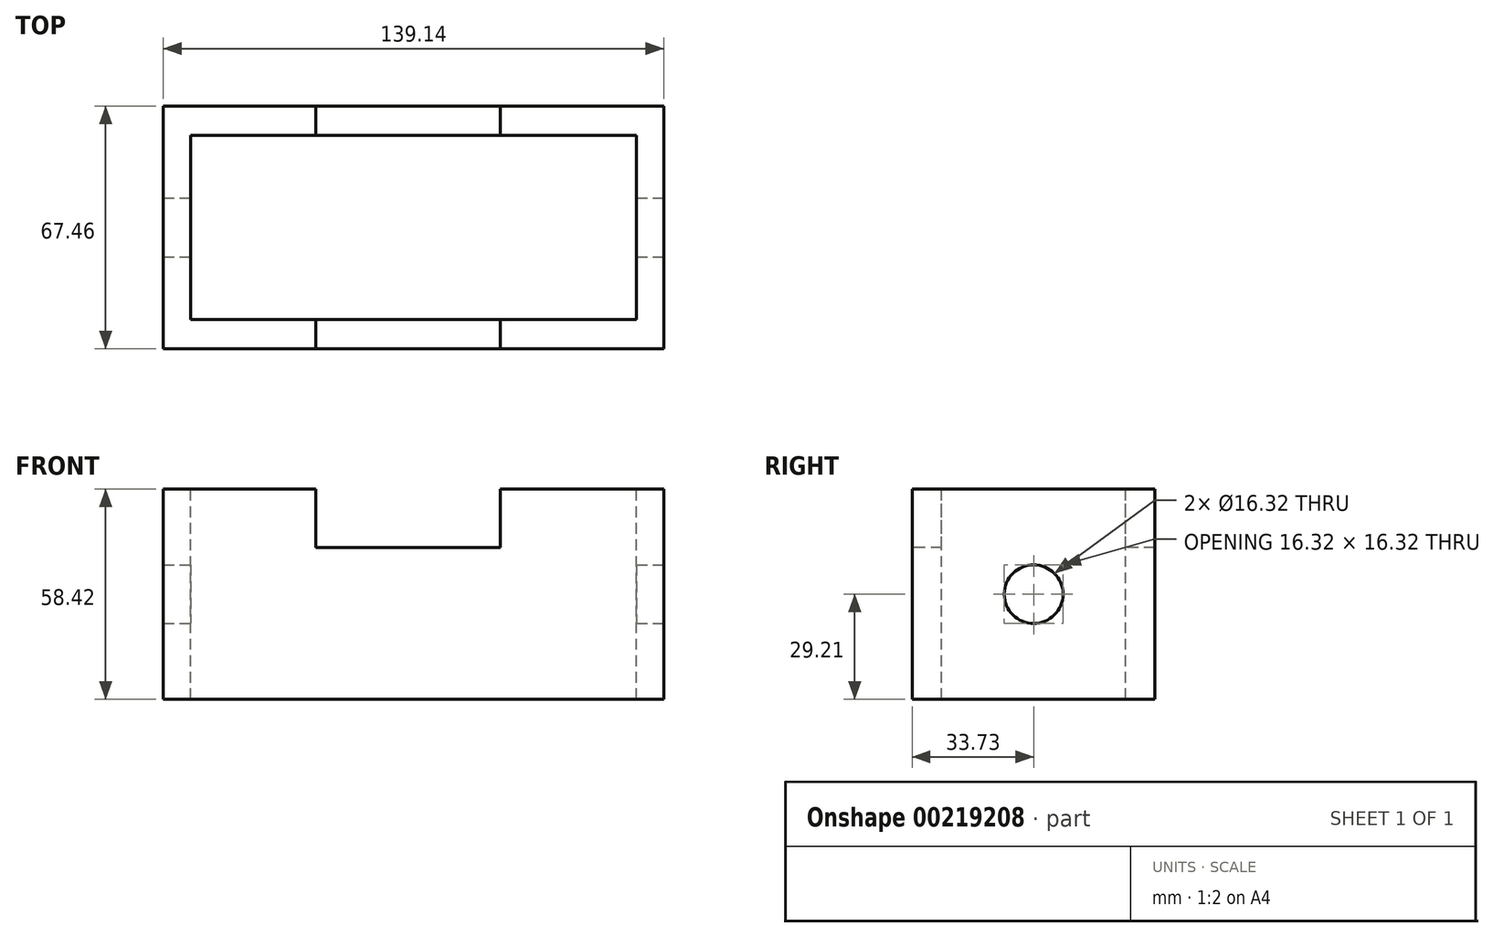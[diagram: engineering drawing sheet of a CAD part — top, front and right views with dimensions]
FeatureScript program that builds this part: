
annotation { "Feature Type Name" : "Feature", "Feature Type Description" : "" }
export const myFeature = defineFeature(function(context is Context, id is Id, definition is map)
    precondition{}
    {
        {
            var Q0;
            Q0=qCreatedBy(makeId("Top.planeOp"),FACE);
            var sketch = newSketch(context, id + "F0", { "sketchPlane" : qUnion([Q0])});
            skLineSegment(sketch, "E0.bottom", {"start": v(69.57, 33.73) * mm, "end": v(-69.57, 33.73) * mm});
            skLineSegment(sketch, "E0.top", {"start": v(69.57, -33.73) * mm, "end": v(-69.57, -33.73) * mm});
            skLineSegment(sketch, "E0.left", {"start": v(69.57, 33.73) * mm, "end": v(69.57, -33.73) * mm});
            skLineSegment(sketch, "E0.right", {"start": v(-69.57, 33.73) * mm, "end": v(-69.57, -33.73) * mm});
            skPoint(sketch, "E0.middle", {"position": v(0, 0) * mm});
            skSolve(sketch);
        }
        {
            var Q0;
            Q0 = qSketchRegion(id + "F0", true);
            extrude(context, id + "F1", {"entities" : qUnion([Q0]), "depth" : 58.42 * mm});
        }
        {
            var Q0;
            Q0=makeQuery(id+"F1.opExtrude","SWEPT_FACE",FACE,{"disambiguationData":[OSD([sQuery(id+"F0.wireOp",EDGE,"E0.left")])]});
            var sketch = newSketch(context, id + "F2", { "sketchPlane" : qUnion([Q0])});
            skCircle(sketch, "E1", {"center": v(0, 29.21) * mm, "radius": 8.16 * mm});
            skPoint(sketch, "E1.centerSnap0", {"position": v(-33.73, 29.21) * mm});
            skSolve(sketch);
        }
        {
            var Q0;
            Q0 = qSketchRegion(id + "F2", true);
            extrude(context, id + "F3", {"entities" : qUnion([Q0]), "operationType" : NewBodyOperationType.REMOVE, "endBound" : BoundingType.THROUGH_ALL, "oppositeDirection" : true, "depth" : 25.4 * mm});
        }
        {
            var Q0;
            Q0=makeQuery(id+"F1.opExtrude","CAP_FACE",FACE,{"disambiguationData":[OSD([sQuery(id+"F0.wireOp",EDGE,"E0.bottom"),sQuery(id+"F0.wireOp",EDGE,"E0.top"),sQuery(id+"F0.wireOp",EDGE,"E0.left"),sQuery(id+"F0.wireOp",EDGE,"E0.right")])],"isStart":false});
            var sketch = newSketch(context, id + "F4", { "sketchPlane" : qUnion([Q0])});
            skLineSegment(sketch, "E2.bottom", {"start": v(62.01, 25.56) * mm, "end": v(-62.01, 25.56) * mm});
            skLineSegment(sketch, "E2.top", {"start": v(62.01, -25.56) * mm, "end": v(-62.01, -25.56) * mm});
            skLineSegment(sketch, "E2.left", {"start": v(62.01, 25.56) * mm, "end": v(62.01, -25.56) * mm});
            skLineSegment(sketch, "E2.right", {"start": v(-62.01, 25.56) * mm, "end": v(-62.01, -25.56) * mm});
            skPoint(sketch, "E2.middle", {"position": v(0, 0) * mm});
            skSolve(sketch);
        }
        {
            var Q0;
            Q0 = qSketchRegion(id + "F4", true);
            extrude(context, id + "F5", {"entities" : qUnion([Q0]), "operationType" : NewBodyOperationType.REMOVE, "endBound" : BoundingType.THROUGH_ALL, "oppositeDirection" : true, "depth" : 25.4 * mm});
        }
        {
            var Q0;
            Q0=makeQuery(id+"F1.opExtrude","SWEPT_FACE",FACE,{"disambiguationData":[OSD([sQuery(id+"F0.wireOp",EDGE,"E0.top")])]});
            var sketch = newSketch(context, id + "F6", { "sketchPlane" : qUnion([Q0])});
            skLineSegment(sketch, "E3.bottom", {"start": v(-27.22, 58.42) * mm, "end": v(24.2, 58.42) * mm});
            skLineSegment(sketch, "E3.top", {"start": v(-27.22, 42.2) * mm, "end": v(24.2, 42.2) * mm});
            skLineSegment(sketch, "E3.left", {"start": v(-27.22, 58.42) * mm, "end": v(-27.22, 42.2) * mm});
            skLineSegment(sketch, "E3.right", {"start": v(24.2, 58.42) * mm, "end": v(24.2, 42.2) * mm});
            skSolve(sketch);
        }
        {
            var Q0;
            Q0 = qSketchRegion(id + "F6", true);
            extrude(context, id + "F7", {"entities" : qUnion([Q0]), "operationType" : NewBodyOperationType.REMOVE, "endBound" : BoundingType.THROUGH_ALL, "oppositeDirection" : true, "depth" : 25.4 * mm});
        }
    });
